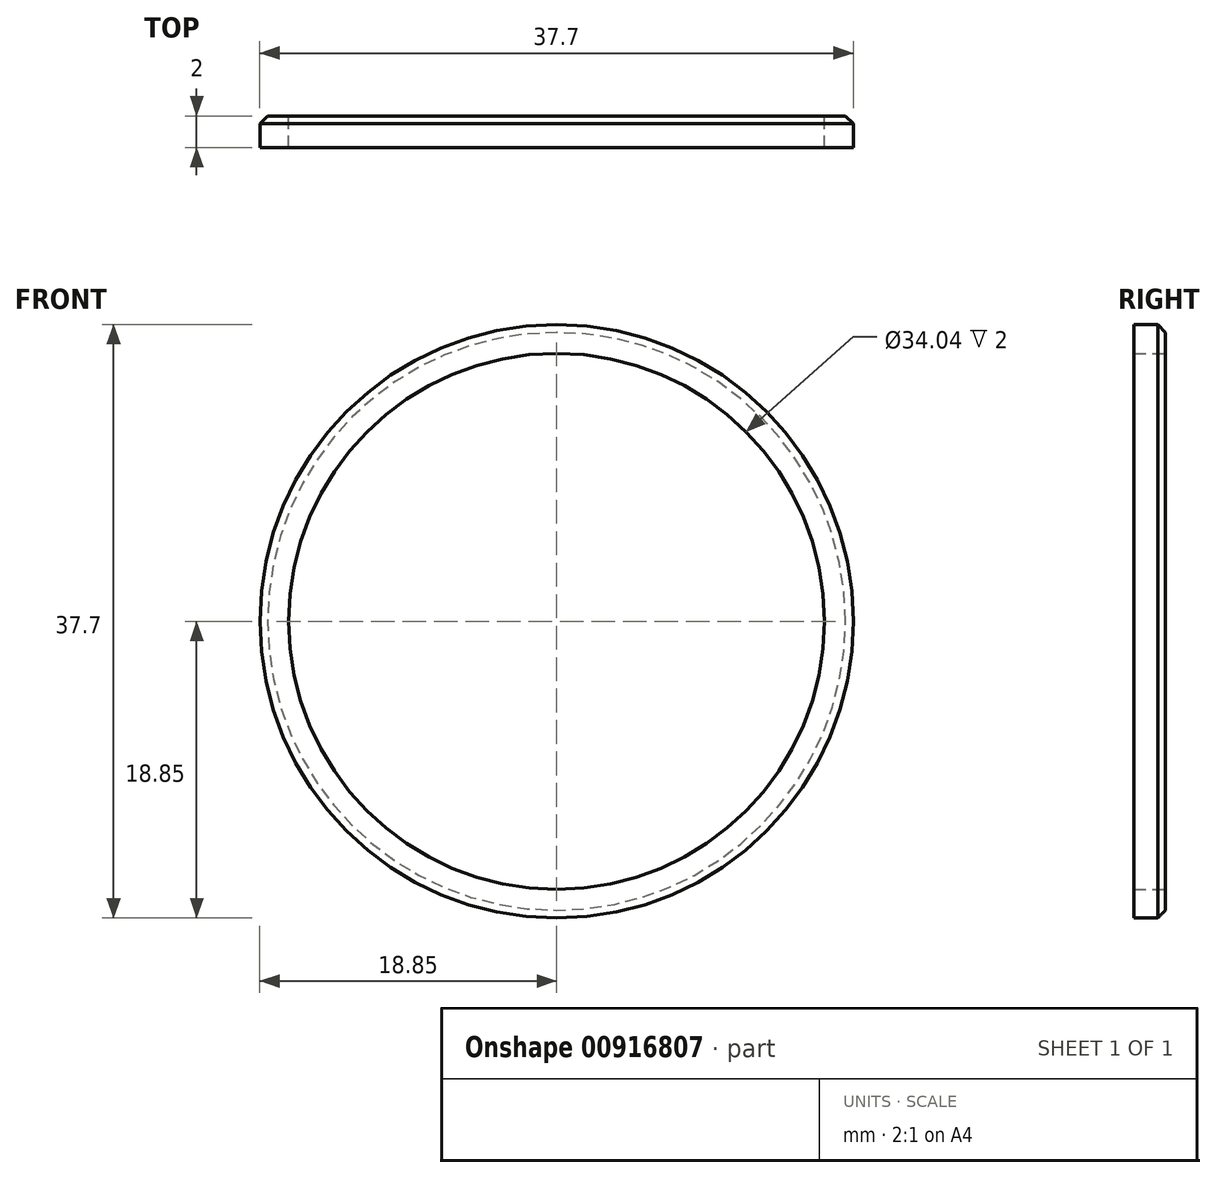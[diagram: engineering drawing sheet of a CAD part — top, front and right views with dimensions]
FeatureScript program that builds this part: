
annotation { "Feature Type Name" : "Feature", "Feature Type Description" : "" }
export const myFeature = defineFeature(function(context is Context, id is Id, definition is map)
    precondition{}
    {
        {
            var Q0;
            Q0=qCreatedBy(makeId("Front.planeOp"),FACE);
            var sketch = newSketch(context, id + "F0", { "sketchPlane" : qUnion([Q0])});
            skCircle(sketch, "E0", {"center": v(0, 0) * mm, "radius": 18.85 * mm});
            skCircle(sketch, "E1", {"center": v(0, 0) * mm, "radius": 17.02 * mm});
            skSolve(sketch);
        }
        {
            var Q0;
            Q0=makeQuery(id+"F0.imprint","IMPRINT",FACE,{"disambiguationData":[TD([[makeQuery(id+"F0.imprint","IMPRINT",EDGE,{"derivedFrom":sQuery(id+"F0.wireOp",EDGE,"E1")}),1.0]])]});
            var Q1;
            Q1=makeQuery(id+"F0.imprint","IMPRINT",FACE,{"disambiguationData":[TD([[makeQuery(id+"F0.imprint","IMPRINT",EDGE,{"derivedFrom":sQuery(id+"F0.wireOp",EDGE,"E0")}),1.0]])]});
            extrude(context, id + "F1", {"entities" : qUnion([Q0, Q1]), "depth" : 2 * mm, "offsetDistance" : 25 * mm});
        }
        {
            var Q0;
            Q0=makeQuery(id+"F0.imprint","IMPRINT",FACE,{"disambiguationData":[TD([[makeQuery(id+"F0.imprint","IMPRINT",EDGE,{"derivedFrom":sQuery(id+"F0.wireOp",EDGE,"E1")}),1.0]])]});
            var Q1;
            Q1=sQuery(id+"F0.wireOp",EDGE,"E1");
            extrude(context, id + "F2", {"entities" : qUnion([Q0]), "operationType" : NewBodyOperationType.REMOVE, "surfaceEntities" : qUnion([Q1]), "depth" : 25 * mm, "offsetDistance" : 25 * mm});
        }
        {
            var Q0;
            Q0=makeQuery(id+"F1.opExtrude","CAP_EDGE",EDGE,{"disambiguationData":[OSD([sQuery(id+"F0.wireOp",EDGE,"E0")])],"isStart":true});
            chamfer(context, id + "F3", {"entities" : qUnion([Q0]), "width" : 0.5 * mm, "tangentPropagation" : true});
        }
    });
